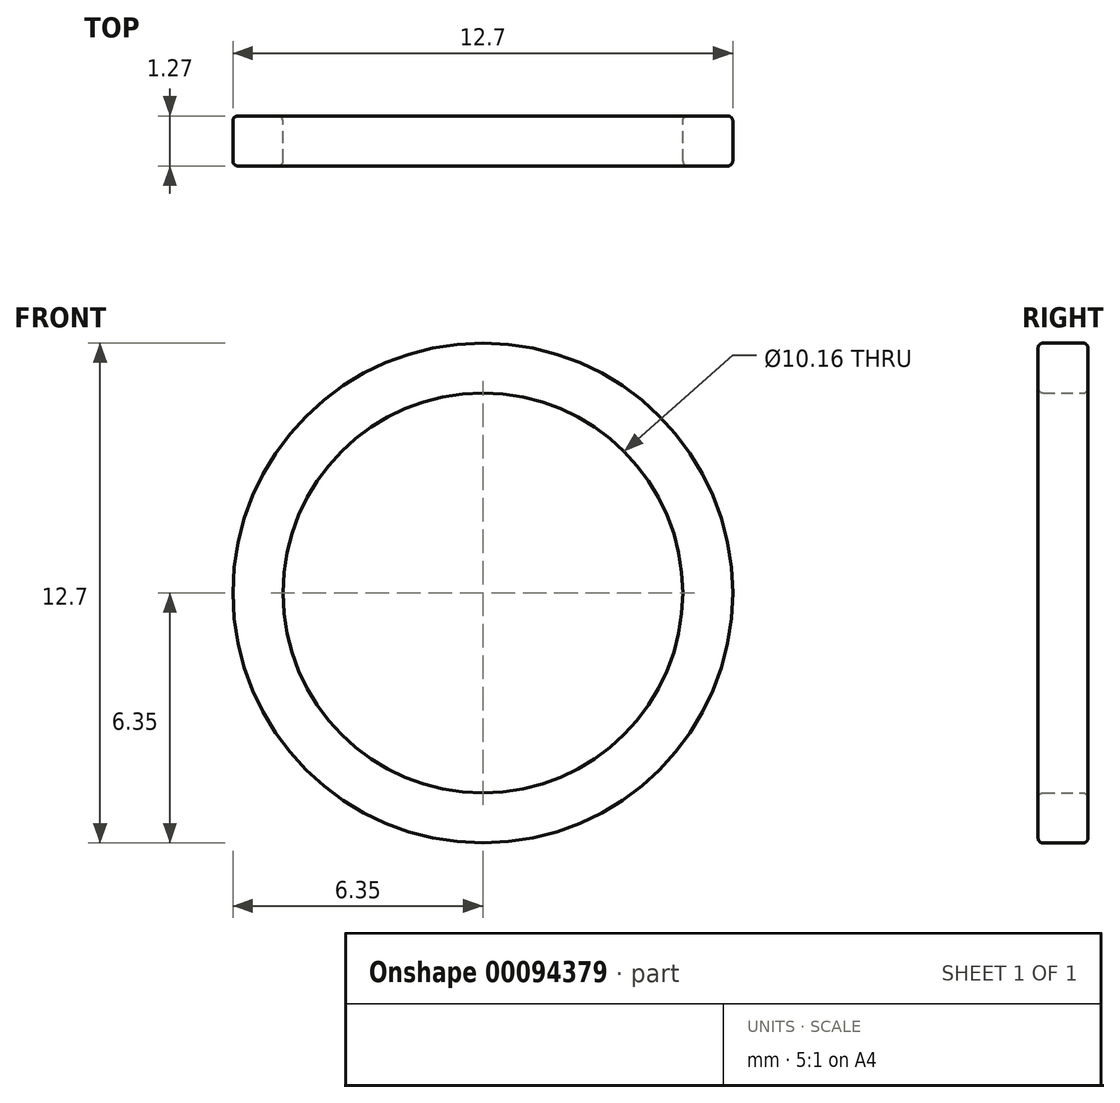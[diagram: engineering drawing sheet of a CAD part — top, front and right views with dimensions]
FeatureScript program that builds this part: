
annotation { "Feature Type Name" : "Feature", "Feature Type Description" : "" }
export const myFeature = defineFeature(function(context is Context, id is Id, definition is map)
    precondition{}
    {
        {
            var Q0;
            Q0=qCreatedBy(makeId("Front.planeOp"),FACE);
            var sketch = newSketch(context, id + "F0", { "sketchPlane" : qUnion([Q0])});
            skCircle(sketch, "E0", {"center": v(0, 0) * mm, "radius": 6.35 * mm});
            skCircle(sketch, "E1", {"center": v(0, 0) * mm, "radius": 5.08 * mm});
            skSolve(sketch);
        }
        {
            var Q0;
            Q0=makeQuery(id+"F0.imprint","IMPRINT",FACE,{"disambiguationData":[TD([[makeQuery(id+"F0.imprint","IMPRINT",EDGE,{"derivedFrom":sQuery(id+"F0.wireOp",EDGE,"E0")}),1.0]])]});
            extrude(context, id + "F1", {"entities" : qUnion([Q0]), "depth" : 1.27 * mm});
        }
        {
            var Q0;
            Q0=makeQuery(id+"F1.opExtrude","CAP_EDGE",EDGE,{"disambiguationData":[OSD([sQuery(id+"F0.wireOp",EDGE,"E0")])],"isStart":false});
            var Q1;
            Q1=makeQuery(id+"F1.opExtrude","CAP_EDGE",EDGE,{"disambiguationData":[OSD([sQuery(id+"F0.wireOp",EDGE,"E0")])],"isStart":true});
            var Q2;
            Q2=makeQuery(id+"F1.opExtrude","CAP_EDGE",EDGE,{"disambiguationData":[OSD([sQuery(id+"F0.wireOp",EDGE,"E1")])],"isStart":false});
            var Q3;
            Q3=makeQuery(id+"F1.opExtrude","CAP_EDGE",EDGE,{"disambiguationData":[OSD([sQuery(id+"F0.wireOp",EDGE,"E1")])],"isStart":true});
            fillet(context, id + "F2", {"entities" : qUnion([Q0, Q1, Q2, Q3]), "radius" : 0.13 * mm, "tangentPropagation" : true, "allowEdgeOverflow" : false});
        }
    });
